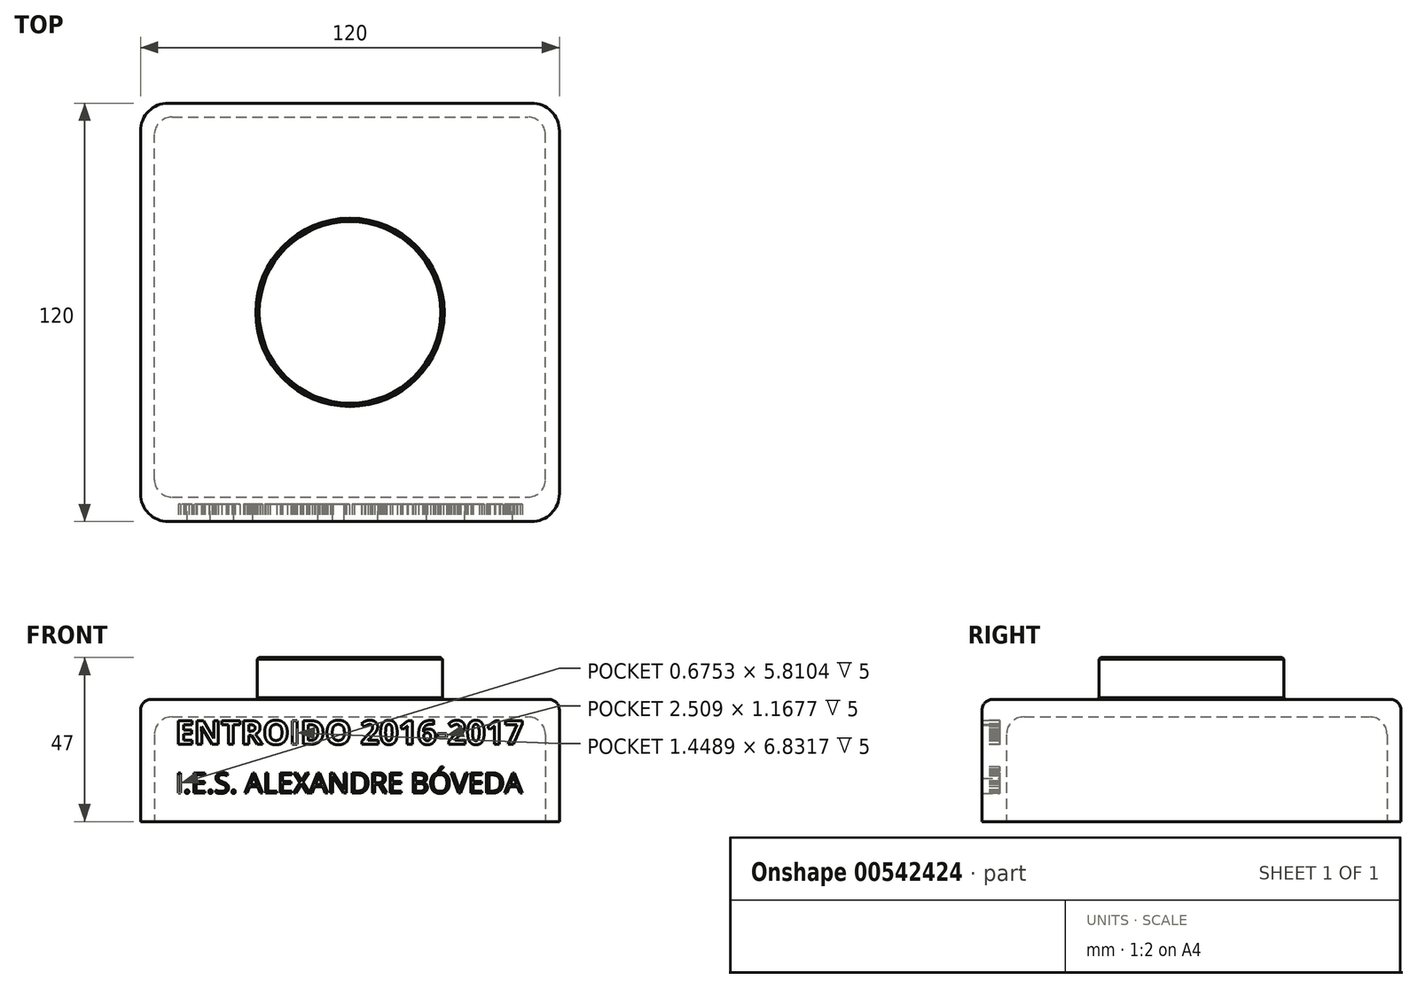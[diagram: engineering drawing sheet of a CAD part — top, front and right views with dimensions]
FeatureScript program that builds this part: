
annotation { "Feature Type Name" : "Feature", "Feature Type Description" : "" }
export const myFeature = defineFeature(function(context is Context, id is Id, definition is map)
    precondition{}
    {
        {
            var Q0;
            Q0=qCreatedBy(makeId("Top.planeOp"),FACE);
            var sketch = newSketch(context, id + "F0", { "sketchPlane" : qUnion([Q0])});
            skLineSegment(sketch, "E0.bottom", {"start": v(60, -60) * mm, "end": v(-60, -60) * mm});
            skLineSegment(sketch, "E0.top", {"start": v(60, 60) * mm, "end": v(-60, 60) * mm});
            skLineSegment(sketch, "E0.left", {"start": v(60, -60) * mm, "end": v(60, 60) * mm});
            skLineSegment(sketch, "E0.right", {"start": v(-60, -60) * mm, "end": v(-60, 60) * mm});
            skPoint(sketch, "E0.middle", {"position": v(0, 0) * mm});
            skSolve(sketch);
        }
        {
            var Q0;
            Q0=makeQuery(id+"F0.imprint","IMPRINT",FACE,{"disambiguationData":[TD([[makeQuery(id+"F0.imprint","IMPRINT",EDGE,{"derivedFrom":sQuery(id+"F0.wireOp",EDGE,"E0.bottom")}),-1.0]])]});
            extrude(context, id + "F1", {"entities" : qUnion([Q0]), "depth" : 35 * mm, "offsetDistance" : 25 * mm});
        }
        {
            var Q0;
            Q0=makeQuery(id+"F1.opExtrude","SWEPT_FACE",FACE,{"disambiguationData":[OSD([sQuery(id+"F0.wireOp",EDGE,"E0.bottom")])]});
            var sketch = newSketch(context, id + "F2", { "sketchPlane" : qUnion([Q0])});
            skText(sketch, "E1", { "text": "ENTROIDO 2016-2017", "fontName": "OpenSans-Bold.ttf"});
            skText(sketch, "E2", { "text": "I.E.S. ALEXANDRE BÓVEDA", "fontName": "OpenSans-Regular.ttf"});
            const initialGuessF2  = {"E1": [-0.05, 0.02211, 1, 0, 0.00689], "E2": [-0.05, 0.00814, 1, 0, 0.00586]};
            skSetInitialGuess(sketch, initialGuessF2);
            skSolve(sketch);
        }
        {
            var Q0;
            Q0 = qSketchRegion(id + "F2", true);
            extrude(context, id + "F3", {"entities" : qUnion([Q0]), "operationType" : NewBodyOperationType.REMOVE, "oppositeDirection" : true, "depth" : 5 * mm, "offsetDistance" : 25 * mm});
        }
        {
            var Q0;
            Q0=makeQuery(id+"F1.opExtrude","SWEPT_EDGE",EDGE,{"disambiguationData":[OSD([sQuery(id+"F0.wireOp",EDGE,"E0.bottom"),sQuery(id+"F0.wireOp",EDGE,"E0.left")])]});
            var Q1;
            Q1=makeQuery(id+"F1.opExtrude","SWEPT_EDGE",EDGE,{"disambiguationData":[OSD([sQuery(id+"F0.wireOp",EDGE,"E0.bottom"),sQuery(id+"F0.wireOp",EDGE,"E0.right")])]});
            var Q2;
            Q2=makeQuery(id+"F1.opExtrude","SWEPT_EDGE",EDGE,{"disambiguationData":[OSD([sQuery(id+"F0.wireOp",EDGE,"E0.top"),sQuery(id+"F0.wireOp",EDGE,"E0.left")])]});
            var Q3;
            Q3=makeQuery(id+"F1.opExtrude","SWEPT_EDGE",EDGE,{"disambiguationData":[OSD([sQuery(id+"F0.wireOp",EDGE,"E0.top"),sQuery(id+"F0.wireOp",EDGE,"E0.right")])]});
            fillet(context, id + "F4", {"entities" : qUnion([Q0, Q1, Q2, Q3]), "radius" : 8 * mm, "tangentPropagation" : true, "allowEdgeOverflow" : false});
        }
        {
            var Q0;
            Q0=makeQuery(id+"F1.opExtrude","CAP_EDGE",EDGE,{"disambiguationData":[OSD([sQuery(id+"F0.wireOp",EDGE,"E0.right")])],"isStart":false});
            var Q1;
            Q1=makeQuery(id+"F1.opExtrude","CAP_FACE",FACE,{"disambiguationData":[OSD([sQuery(id+"F0.wireOp",EDGE,"E0.bottom"),sQuery(id+"F0.wireOp",EDGE,"E0.top"),sQuery(id+"F0.wireOp",EDGE,"E0.left"),sQuery(id+"F0.wireOp",EDGE,"E0.right")])],"isStart":false});
            fillet(context, id + "F5", {"entities" : qUnion([Q0, Q1]), "radius" : 3 * mm, "tangentPropagation" : true, "allowEdgeOverflow" : false});
        }
        {
            var Q0;
            Q0=makeQuery(id+"F1.opExtrude","CAP_FACE",FACE,{"disambiguationData":[OSD([sQuery(id+"F0.wireOp",EDGE,"E0.bottom"),sQuery(id+"F0.wireOp",EDGE,"E0.top"),sQuery(id+"F0.wireOp",EDGE,"E0.left"),sQuery(id+"F0.wireOp",EDGE,"E0.right")])],"isStart":false});
            var sketch = newSketch(context, id + "F6", { "sketchPlane" : qUnion([Q0])});
            skCircle(sketch, "E3", {"center": v(0, 0) * mm, "radius": 26.5 * mm});
            skSolve(sketch);
        }
        {
            var Q0;
            Q0=makeQuery(id+"F6.imprint","IMPRINT",FACE,{"disambiguationData":[TD([[makeQuery(id+"F6.imprint","IMPRINT",EDGE,{"derivedFrom":sQuery(id+"F6.wireOp",EDGE,"E3")}),1.0]])]});
            extrude(context, id + "F7", {"entities" : qUnion([Q0]), "operationType" : NewBodyOperationType.ADD, "depth" : 12 * mm, "offsetDistance" : 25 * mm});
        }
        {
            var Q0;
            Q0=makeQuery(id+"F7.opExtrude","CAP_EDGE",EDGE,{"disambiguationData":[OSD([sQuery(id+"F6.wireOp",EDGE,"E3")])],"isStart":false});
            var Q1;
            Q1=makeQuery(id+"F1.opExtrude","CAP_FACE",FACE,{"disambiguationData":[OSD([sQuery(id+"F0.wireOp",EDGE,"E0.bottom"),sQuery(id+"F0.wireOp",EDGE,"E0.top"),sQuery(id+"F0.wireOp",EDGE,"E0.left"),sQuery(id+"F0.wireOp",EDGE,"E0.right")])],"isStart":false});
            chamfer(context, id + "F8", {"entities" : qUnion([Q0, Q1]), "width" : 0.5 * mm, "tangentPropagation" : true});
        }
        {
            var Q0;
            Q0=makeQuery(id+"F1.opExtrude","CAP_FACE",FACE,{"disambiguationData":[OSD([sQuery(id+"F0.wireOp",EDGE,"E0.bottom"),sQuery(id+"F0.wireOp",EDGE,"E0.top"),sQuery(id+"F0.wireOp",EDGE,"E0.left"),sQuery(id+"F0.wireOp",EDGE,"E0.right")])],"isStart":true});
            var sketch = newSketch(context, id + "F9", { "sketchPlane" : qUnion([Q0])});
            skLineSegment(sketch, "E4.bottom", {"start": v(-51, 53) * mm, "end": v(51, 53) * mm});
            skLineSegment(sketch, "E4.top", {"start": v(-51, -56) * mm, "end": v(51, -56) * mm});
            skLineSegment(sketch, "E4.left", {"start": v(-56, 48) * mm, "end": v(-56, -51) * mm});
            skLineSegment(sketch, "E4.right", {"start": v(56, 48) * mm, "end": v(56, -51) * mm});
            skPoint(sketch, "E5.visualSharp", {"position": v(56, 53) * mm});
            skArc(sketch, "E5.filletArc", {"start": v(56, 48) * mm, "mid": v(54.54, 51.54) * mm, "end": v(51, 53) * mm});
            skPoint(sketch, "E6.visualSharp", {"position": v(56, -56) * mm});
            skArc(sketch, "E6.filletArc", {"start": v(51, -56) * mm, "mid": v(54.54, -54.54) * mm, "end": v(56, -51) * mm});
            skPoint(sketch, "E7.visualSharp", {"position": v(-56, -56) * mm});
            skArc(sketch, "E7.filletArc", {"start": v(-56, -51) * mm, "mid": v(-54.54, -54.54) * mm, "end": v(-51, -56) * mm});
            skPoint(sketch, "E8.visualSharp", {"position": v(-56, 53) * mm});
            skArc(sketch, "E8.filletArc", {"start": v(-51, 53) * mm, "mid": v(-54.54, 51.54) * mm, "end": v(-56, 48) * mm});
            skSolve(sketch);
        }
        {
            var Q0;
            Q0 = qSketchRegion(id + "F9", true);
            extrude(context, id + "F10", {"entities" : qUnion([Q0]), "operationType" : NewBodyOperationType.REMOVE, "oppositeDirection" : true, "depth" : 30 * mm, "offsetDistance" : 25 * mm});
        }
        {
            var Q0;
            Q0=makeQuery(id+"F10.boolean.opBoolean","COPY",EDGE,{"derivedFrom":makeQuery(id+"F10.opExtrude","CAP_EDGE",EDGE,{"disambiguationData":[OSD([sQuery(id+"F9.wireOp",EDGE,"E4.top")])],"isStart":false})});
            fillet(context, id + "F11", {"entities" : qUnion([Q0]), "radius" : 5 * mm, "tangentPropagation" : true, "allowEdgeOverflow" : false});
        }
    });
